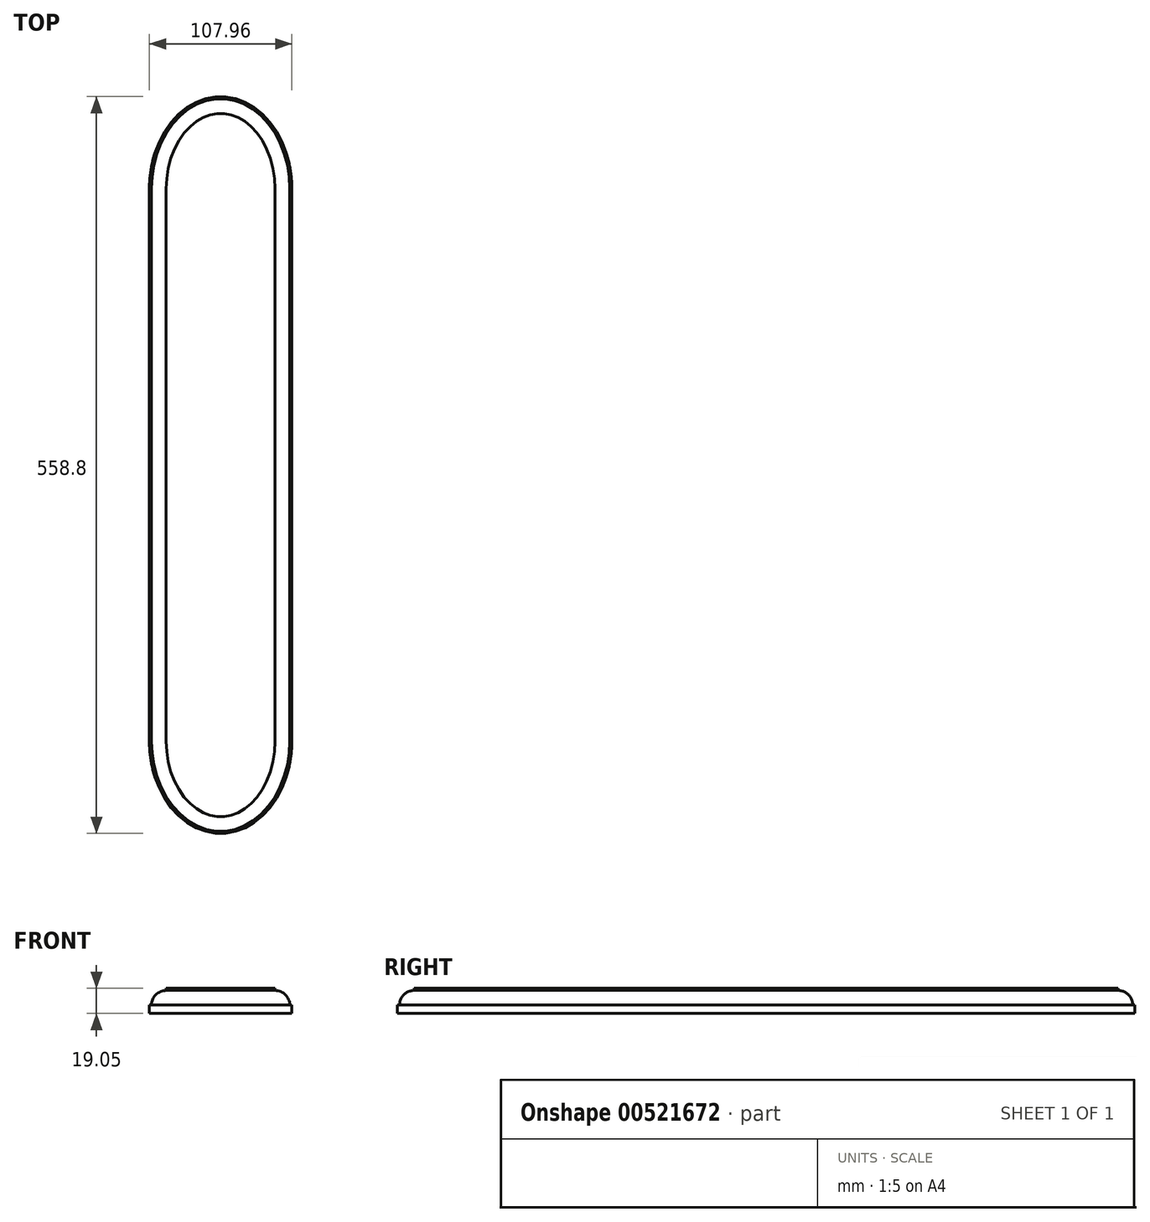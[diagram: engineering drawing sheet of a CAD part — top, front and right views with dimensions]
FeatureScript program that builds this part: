
annotation { "Feature Type Name" : "Feature", "Feature Type Description" : "" }
export const myFeature = defineFeature(function(context is Context, id is Id, definition is map)
    precondition{}
    {
        {
            var Q0;
            Q0=qCreatedBy(makeId("Top.planeOp"),FACE);
            var sketch = newSketch(context, id + "F0", { "sketchPlane" : qUnion([Q0])});
            skLineSegment(sketch, "E0.left", {"start": v(53.98, 0) * mm, "end": v(53.98, -419.1) * mm});
            skLineSegment(sketch, "E0.right", {"start": v(-53.98, 0) * mm, "end": v(-53.98, -419.1) * mm});
            skPoint(sketch, "E0.middle", {"position": v(0, 0) * mm});
            skEllipticalArc(sketch, "E1", {});
            skEllipticalArc(sketch, "E2", {});
            const initialGuessF0  = {"E1": [0, 0, 0, 1, 0.06985, 0.053975, 4.71238898038469, 1.5707963267948966], "E2": [0, -0.4191, 0, -1, 0.06985, 0.053975, 4.71238898038469, 1.5707963267948966]};
            skSetInitialGuess(sketch, initialGuessF0);
            skSolve(sketch);
        }
        {
            var Q0;
            Q0 = qSketchRegion(id + "F0", true);
            extrude(context, id + "F1", {"entities" : qUnion([Q0]), "depth" : 19.05 * mm, "offsetDistance" : 25.4 * mm});
        }
        {
            var Q0;
            Q0=qCreatedBy(makeId("Front.planeOp"),FACE);
            var sketch = newSketch(context, id + "F2", { "sketchPlane" : qUnion([Q0])});
            skArc(sketch, "E3", {"start": v(-41.27, 17.46) * mm, "mid": v(-49.13, 14.2) * mm, "end": v(-52.39, 6.35) * mm});
            skLineSegment(sketch, "E4.bottom", {"start": v(-41.27, 6.35) * mm, "end": v(-53.97, 6.35) * mm, "construction": true});
            skLineSegment(sketch, "E4.top", {"start": v(-41.27, 19.05) * mm, "end": v(-53.97, 19.05) * mm});
            skLineSegment(sketch, "E4.right", {"start": v(-53.97, 6.35) * mm, "end": v(-53.97, 19.05) * mm});
            skLineSegment(sketch, "E5", {"start": v(-41.27, 19.05) * mm, "end": v(-41.27, 6.35) * mm, "construction": true});
            skLineSegment(sketch, "E6", {"start": v(-41.27, 17.46) * mm, "end": v(-41.27, 19.05) * mm});
            skLineSegment(sketch, "E7", {"start": v(-52.39, 6.35) * mm, "end": v(-53.97, 6.35) * mm});
            skSolve(sketch);
        }
        {
            var Q0;
            Q0 = qSketchRegion(id + "F2", true);
            var Q1;
            Q1=makeQuery(id+"F1.opExtrude","CAP_EDGE",EDGE,{"disambiguationData":[OSD([sQuery(id+"F0.wireOp",EDGE,"E0.right")])],"isStart":false});
            var Q2;
            Q2=makeQuery(id+"F1.opExtrude","CAP_EDGE",EDGE,{"disambiguationData":[OSD([sQuery(id+"F0.wireOp",EDGE,"E2")])],"isStart":false});
            var Q3;
            Q3=makeQuery(id+"F1.opExtrude","CAP_EDGE",EDGE,{"disambiguationData":[OSD([sQuery(id+"F0.wireOp",EDGE,"E0.left")])],"isStart":false});
            var Q4;
            Q4=makeQuery(id+"F1.opExtrude","CAP_EDGE",EDGE,{"disambiguationData":[OSD([sQuery(id+"F0.wireOp",EDGE,"E1")])],"isStart":false});
            sweep(context, id + "F3", {"operationType" : NewBodyOperationType.REMOVE, "profiles" : qUnion([Q0]), "path" : qUnion([Q1, Q2, Q3, Q4])});
        }
    });
